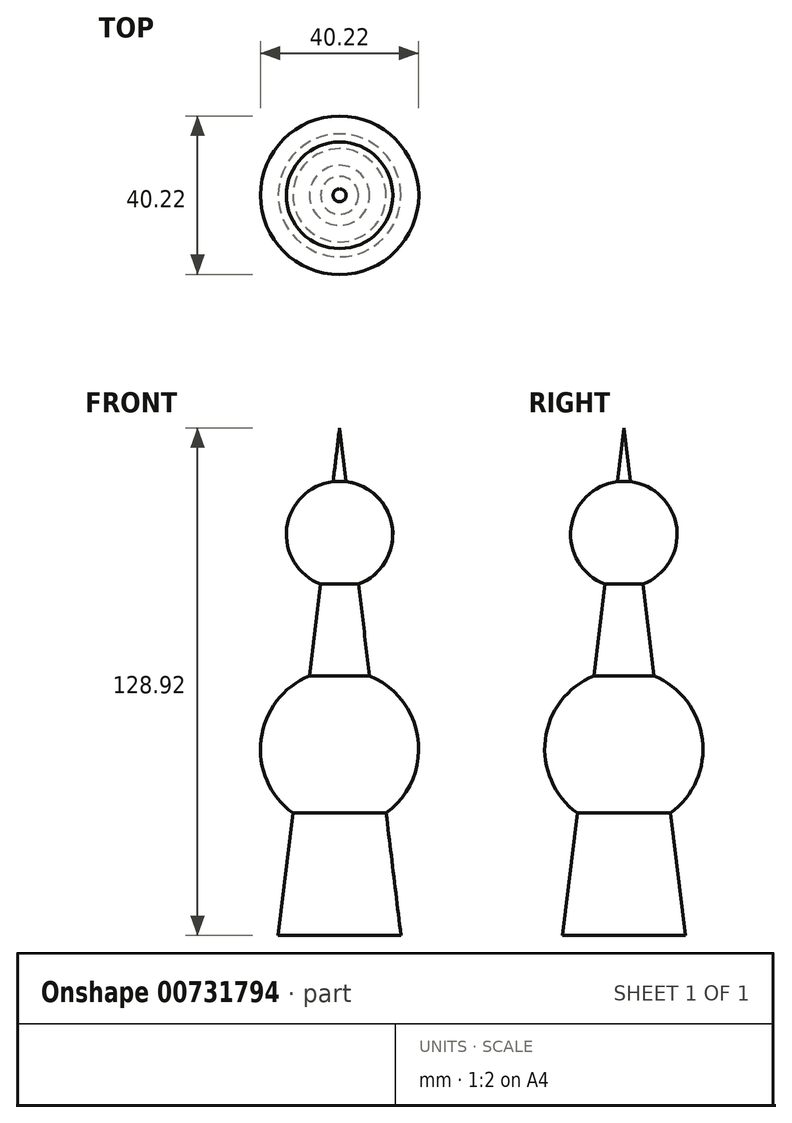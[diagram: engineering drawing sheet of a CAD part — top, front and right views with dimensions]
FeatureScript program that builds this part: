
annotation { "Feature Type Name" : "Feature", "Feature Type Description" : "" }
export const myFeature = defineFeature(function(context is Context, id is Id, definition is map)
    precondition{}
    {
        {
            var Q0;
            Q0=qCreatedBy(makeId("Front.planeOp"),FACE);
            var sketch = newSketch(context, id + "F0", { "sketchPlane" : qUnion([Q0])});
            skLineSegment(sketch, "E0", {"start": v(0, 0) * mm, "end": v(-15.6, 0) * mm});
            skPoint(sketch, "E1.centerSnap0", {"position": v(-7.8, 37.4) * mm});
            skLineSegment(sketch, "E2", {"start": v(0, 74.81) * mm, "end": v(0, 128.92) * mm});
            skLineSegment(sketch, "E3", {"start": v(0, 128.92) * mm, "end": v(-1.65, 115.29) * mm});
            skArc(sketch, "E4", {"start": v(-1.65, 115.29) * mm, "mid": v(-13.42, 103.49) * mm, "end": v(-4.8, 89.22) * mm});
            skArc(sketch, "E5", {"start": v(-7.62, 65.95) * mm, "mid": v(-19.97, 49.75) * mm, "end": v(-11.83, 31.07) * mm});
            skLineSegment(sketch, "E6", {"start": v(0, 74.81) * mm, "end": v(0, 0) * mm});
            skLineSegment(sketch, "E7.trimOffspring", {"start": v(-4.8, 89.22) * mm, "end": v(-7.62, 65.95) * mm});
            skLineSegment(sketch, "E8.trimOffspring", {"start": v(-11.83, 31.07) * mm, "end": v(-15.6, 0) * mm});
            skSolve(sketch);
        }
        {
            var Q0;
            Q0=makeQuery(id+"F0.imprint","IMPRINT",FACE,{"disambiguationData":[TD([[makeQuery(id+"F0.imprint","IMPRINT",EDGE,{"derivedFrom":sQuery(id+"F0.wireOp",EDGE,"E0")}),-1.0]])]});
            var Q1;
            Q1=sQuery(id+"F0.wireOp",EDGE,"E6");
            revolve(context, id + "F1", {"surfaceOperationType" : NewSurfaceOperationType.NEW, "entities" : qUnion([Q0]), "axis" : qUnion([Q1]), "revolveType" : RevolveType.FULL});
        }
    });
